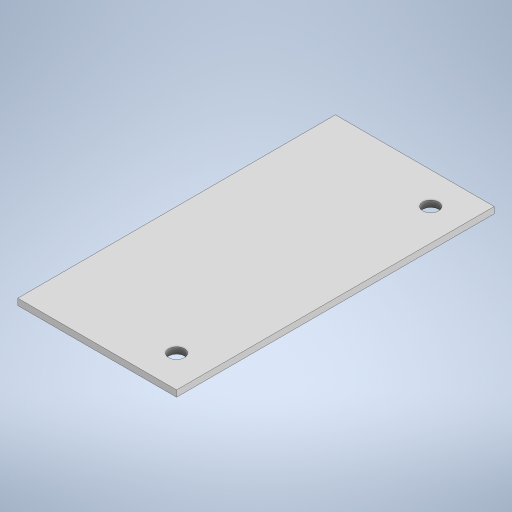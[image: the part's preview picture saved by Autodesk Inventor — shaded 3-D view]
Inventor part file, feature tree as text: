
AUTODESK INVENTOR PART (.ipt)
format: ipt  version: 2023 (Build 270158000, 158)  size: 217,600 bytes
history: native  units: mm
features: extrude x1, sketch x1
ambient origin geometry x8: Origin, YZ Plane, XZ Plane, XY Plane, X Axis, Y Axis, Z Axis, Center Point
bodies: Body1 (feature_tree)
feature tree (2):
  extrude  "Extrusion2"  Depth=100.0mm
  sketch  "Sketch1"  dims[d0=50.0mm d1=100.0mm d8=10.0mm d9=10.0mm d10=5.0mm d11=10.0mm d12=10.0mm d13=5.0mm d14=2.0mm d15=0.0mm]
